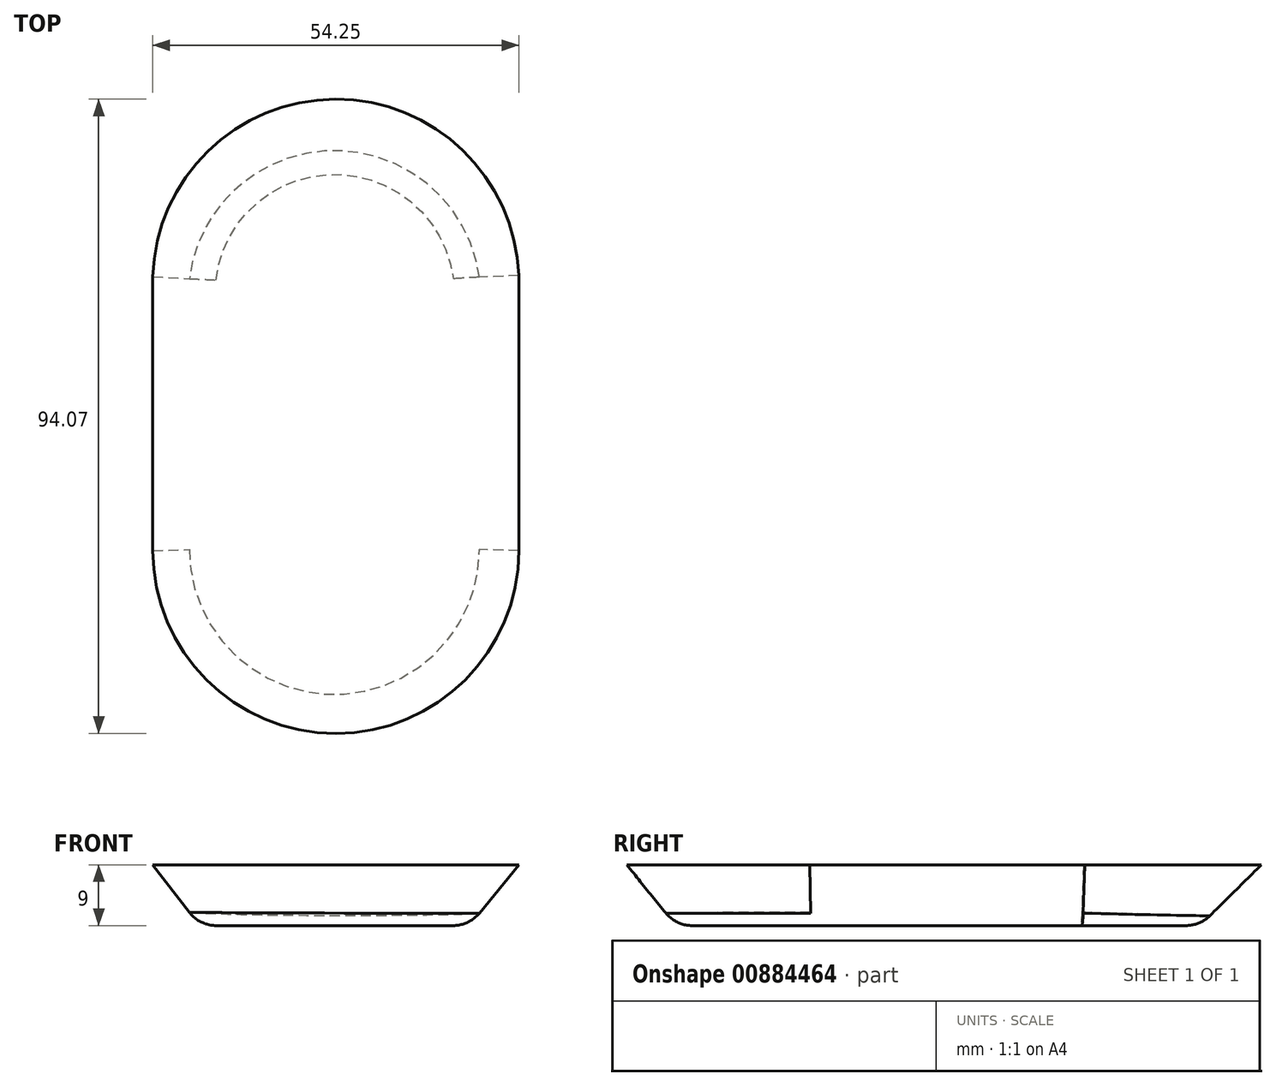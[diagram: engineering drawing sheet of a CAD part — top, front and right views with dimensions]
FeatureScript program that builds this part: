
annotation { "Feature Type Name" : "Feature", "Feature Type Description" : "" }
export const myFeature = defineFeature(function(context is Context, id is Id, definition is map)
    precondition{}
    {
        {
            var Q0;
            Q0=qCreatedBy(makeId("Top.planeOp"),FACE);
            var sketch = newSketch(context, id + "F0", { "sketchPlane" : qUnion([Q0])});
            skArc(sketch, "E0", {"start": v(17.77, 14.67) * mm, "mid": v(-2.33, 32.03) * mm, "end": v(-22.23, 14.44) * mm});
            skLineSegment(sketch, "E1", {"start": v(-22.23, 14.44) * mm, "end": v(-22.23, -25.64) * mm});
            skLineSegment(sketch, "E2", {"start": v(17.77, 14.67) * mm, "end": v(17.77, -25.64) * mm});
            skArc(sketch, "E3", {"start": v(-22.23, -25.64) * mm, "mid": v(-2.23, -45.64) * mm, "end": v(17.77, -25.64) * mm});
            skSolve(sketch);
        }
        {
            var Q0;
            Q0=qCreatedBy(makeId("Top.planeOp"),FACE);
            cPlane(context, id + "F1", {"entities" : qUnion([Q0]), "cplaneType" : CPlaneType.OFFSET, "offset" : 9 * mm, "width" : 150 * mm, "height" : 150 * mm});
        }
        {
            var Q0;
            Q0=qCreatedBy(id+"F1.planeOp",FACE);
            var sketch = newSketch(context, id + "F2", { "sketchPlane" : qUnion([Q0])});
            skArc(sketch, "E4", {"start": v(25.11, 14.96) * mm, "mid": v(-2.1, 41.13) * mm, "end": v(-29.14, 14.79) * mm});
            skLineSegment(sketch, "E5", {"start": v(-29.14, 14.79) * mm, "end": v(-29.14, -25.81) * mm});
            skLineSegment(sketch, "E6", {"start": v(25.11, 14.96) * mm, "end": v(25.11, -25.81) * mm});
            skArc(sketch, "E7", {"start": v(-29.14, -25.81) * mm, "mid": v(-2.01, -52.94) * mm, "end": v(25.11, -25.81) * mm});
            skSolve(sketch);
        }
        {
            var Q0;
            Q0=makeQuery(id+"F2.imprint","IMPRINT",FACE,{"disambiguationData":[TD([[makeQuery(id+"F2.imprint","IMPRINT",EDGE,{"derivedFrom":sQuery(id+"F2.wireOp",EDGE,"E4")}),1.0]])]});
            var Q1;
            Q1=makeQuery(id+"F0.imprint","IMPRINT",FACE,{"disambiguationData":[TD([[makeQuery(id+"F0.imprint","IMPRINT",EDGE,{"derivedFrom":sQuery(id+"F0.wireOp",EDGE,"E0")}),1.0]])]});
            loft(context, id + "F3", {"sheetProfilesArray" : [{ "sheetProfileEntities" : qUnion([Q0]) }, { "sheetProfileEntities" : qUnion([Q1]) }]});
        }
        {
            var Q0;
            Q0=makeQuery(id+"F3.opLoft","MID_CAP_EDGE",EDGE,{"disambiguationData":[OSD([sQuery(id+"F0.wireOp",EDGE,"E1"),sQuery(id+"F0.wireOp",EDGE,"E2"),sQuery(id+"F0.wireOp",EDGE,"E3")])],"capPos":1.0});
            var Q1;
            Q1=makeQuery(id+"F3.opLoft","MID_CAP_EDGE",EDGE,{"disambiguationData":[OSD([sQuery(id+"F0.wireOp",EDGE,"E0"),sQuery(id+"F0.wireOp",EDGE,"E1"),sQuery(id+"F0.wireOp",EDGE,"E2")])],"capPos":1.0});
            fillet(context, id + "F4", {"entities" : qUnion([Q0, Q1]), "radius" : 5 * mm, "tangentPropagation" : true, "allowEdgeOverflow" : false});
        }
    });
